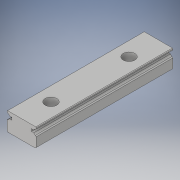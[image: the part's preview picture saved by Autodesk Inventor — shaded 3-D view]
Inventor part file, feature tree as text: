
AUTODESK INVENTOR PART (.ipt)
format: ipt  version: 2019 (Build 230136000, 136)  size: 157,696 bytes
history: native  units: mm
features: other x7, sketch x2, extrude x1, hole x1, pattern_linear x1
ambient origin geometry x8: Origin, YZ Plane, XZ Plane, XY Plane, X Axis, Y Axis, Z Axis, Center Point
bodies: Solid1 (feature_tree)
feature tree (12):
  extrude  "Extrusion1"  Depth=10.0mm TaperAngle=0.0deg
  hole  "Hole1"  [1 undecoded]
  pattern_linear  "Rectangular Pattern1"  [2 undecoded]
  other  "to_block_XY"
  other  "to_block_YZ"
  other  "to_block_ZX"
  other  "to_block_X"
  other  "to_block_Y"
  other  "to_block_Z"
  other  "to_block_Center"
  sketch  "Sketch_12"  dims[d2=3.5mm d3=6.0mm d4=6.0mm d5=4.5mm d6=90.0deg d7=9.5mm d8=0.0mm d9=20.0mm d11=40.0mm d12=10.0mm d14=0.0mm]
  sketch  "Sketch2"  dims[d0=70.0mm d1=0.0mm]
note: 3 required parameter values undecoded (feature->parameter linkage not recoverable at this tier; creation-order binding heuristic only, values carry confidence <= 0.55)
